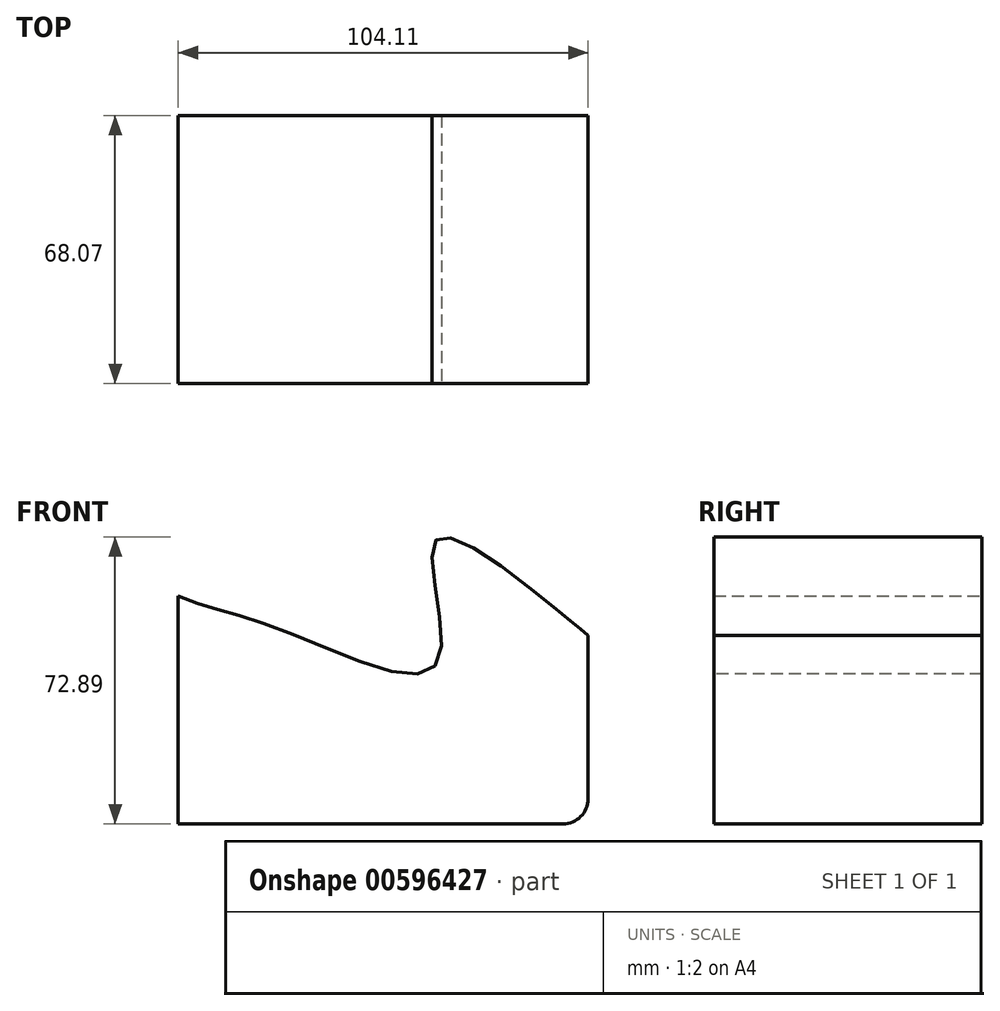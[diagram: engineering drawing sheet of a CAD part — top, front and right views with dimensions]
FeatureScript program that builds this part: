
annotation { "Feature Type Name" : "Feature", "Feature Type Description" : "" }
export const myFeature = defineFeature(function(context is Context, id is Id, definition is map)
    precondition{}
    {
        {
            var Q0;
            Q0=qCreatedBy(makeId("Front.planeOp"),FACE);
            var sketch = newSketch(context, id + "F0", { "sketchPlane" : qUnion([Q0])});
            skLineSegment(sketch, "E0.bottom", {"start": v(-59.27, 57.2) * mm, "end": v(32.14, 57.2) * mm});
            skLineSegment(sketch, "E0.top", {"start": v(-65.62, -101.99) * mm, "end": v(32.14, -101.99) * mm});
            skLineSegment(sketch, "E0.left", {"start": v(-65.62, 50.84) * mm, "end": v(-65.62, -101.99) * mm});
            skLineSegment(sketch, "E0.right", {"start": v(38.5, 50.84) * mm, "end": v(38.5, -95.64) * mm});
            skPoint(sketch, "E1.visualSharp", {"position": v(-65.62, 57.2) * mm});
            skArc(sketch, "E1.filletArc", {"start": v(-59.27, 57.2) * mm, "mid": v(-63.76, 55.33) * mm, "end": v(-65.62, 50.84) * mm});
            skPoint(sketch, "E2.visualSharp", {"position": v(38.5, 57.2) * mm});
            skArc(sketch, "E2.filletArc", {"start": v(38.5, 50.84) * mm, "mid": v(36.63, 55.33) * mm, "end": v(32.14, 57.2) * mm});
            skPoint(sketch, "E3.visualSharp", {"position": v(38.5, -101.99) * mm});
            skArc(sketch, "E3.filletArc", {"start": v(32.14, -101.99) * mm, "mid": v(36.63, -100.13) * mm, "end": v(38.5, -95.64) * mm});
            skFitSpline(sketch, "E4", {"points": [v(-65.62, 6.04) * mm, v(-16, -1.18) * mm, v(-23.57, -14.12) * mm, v(38.5, -15.8) * mm], "startDerivative": vector(204.86, 85.19) * mm, "endDerivative": vector(91.94, -40.14) * mm});
            skFitSpline(sketch, "E5", {"points": [v(-65.62, -44.04) * mm, v(-40.2, -52.36) * mm, v(0, -61.36) * mm, v(0, -29.74) * mm, v(31.52, -48.4) * mm, v(38.5, -54.16) * mm], "startDerivative": vector(116.28, -54.82) * mm, "endDerivative": vector(42.88, -41.4) * mm});
            skSolve(sketch);
        }
        {
            var Q0;
            {var subQ4=sQuery(id+"F0.wireOp",EDGE,"E0.top");Q0=makeQuery(id+"F0.imprint","IMPRINT",FACE,{"disambiguationData":[TD([[makeQuery(id+"F0.imprint","IMPRINT",EDGE,{"derivedFrom":subQ4}),1.0]])]});}
            extrude(context, id + "F1", {"entities" : qUnion([Q0]), "depth" : 68.07 * mm, "offsetDistance" : 25.4 * mm});
        }
    });
